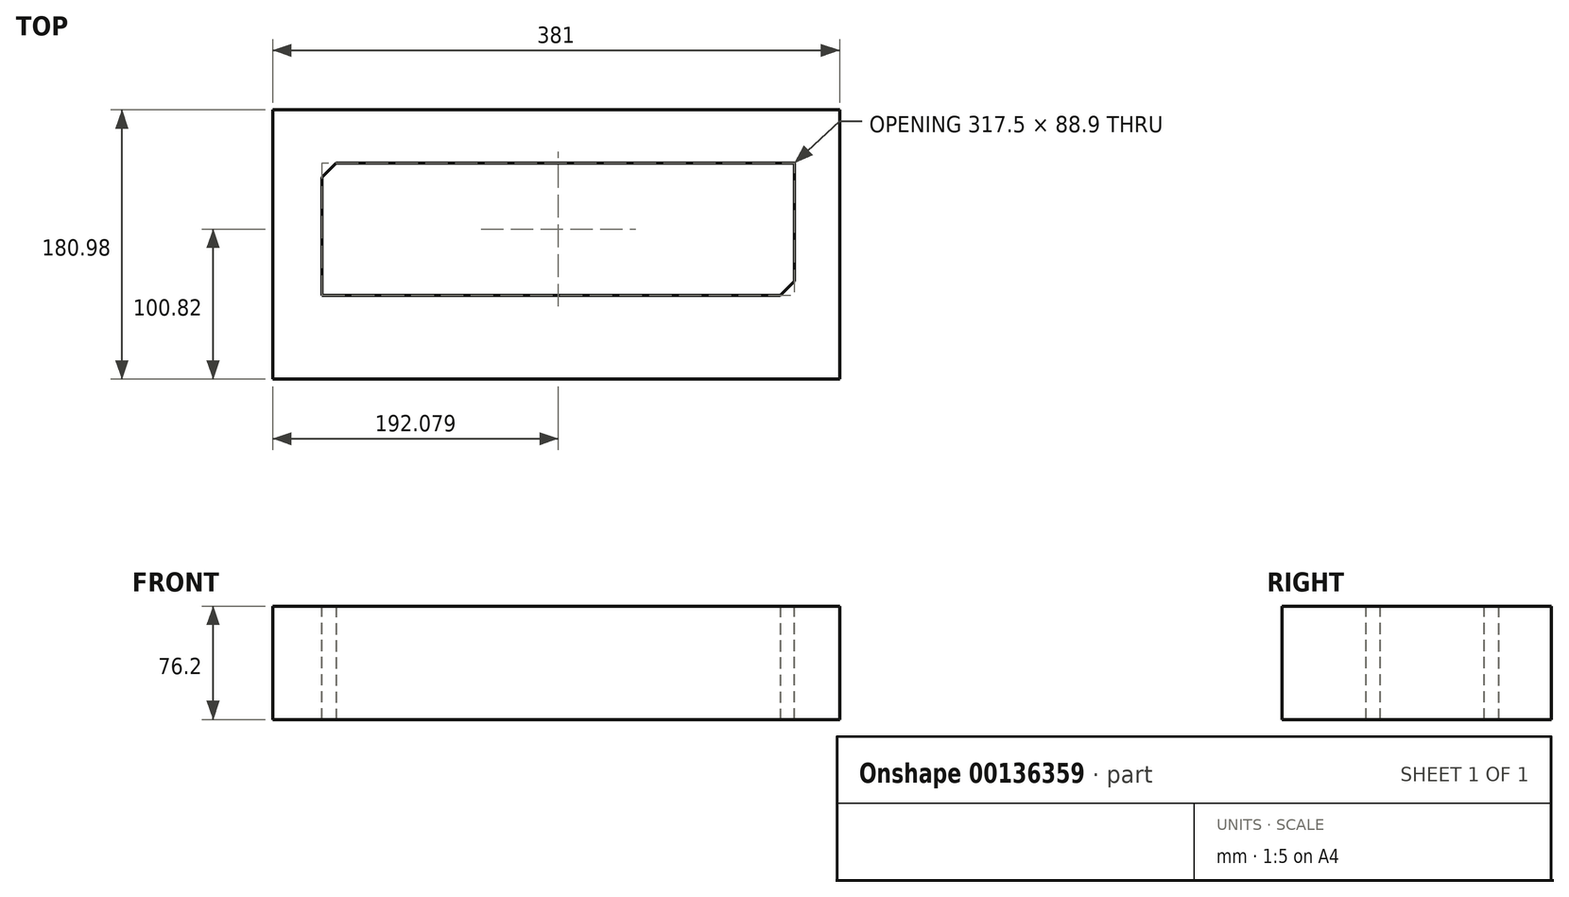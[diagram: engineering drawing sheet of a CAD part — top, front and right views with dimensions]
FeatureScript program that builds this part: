
annotation { "Feature Type Name" : "Feature", "Feature Type Description" : "" }
export const myFeature = defineFeature(function(context is Context, id is Id, definition is map)
    precondition{}
    {
        {
            var Q0;
            Q0=qCreatedBy(makeId("Top.planeOp"),FACE);
            var sketch = newSketch(context, id + "F0", { "sketchPlane" : qUnion([Q0])});
            skLineSegment(sketch, "E0", {"start": v(-193.33, 124.6) * mm, "end": v(187.67, 124.6) * mm});
            skLineSegment(sketch, "E1", {"start": v(187.67, 124.6) * mm, "end": v(187.67, -56.37) * mm});
            skLineSegment(sketch, "E2", {"start": v(187.67, -56.37) * mm, "end": v(-193.33, -56.37) * mm});
            skLineSegment(sketch, "E3", {"start": v(-193.33, -56.37) * mm, "end": v(-193.33, 124.6) * mm});
            skSolve(sketch);
        }
        {
            var Q0;
            Q0 = qSketchRegion(id + "F0", true);
            extrude(context, id + "F1", {"entities" : qUnion([Q0]), "depth" : 76.2 * mm});
        }
        {
            var Q0;
            Q0=makeQuery(id+"F1.opExtrude","CAP_FACE",FACE,{"disambiguationData":[OSD([sQuery(id+"F0.wireOp",EDGE,"E0"),sQuery(id+"F0.wireOp",EDGE,"E1"),sQuery(id+"F0.wireOp",EDGE,"E2"),sQuery(id+"F0.wireOp",EDGE,"E3")])],"isStart":false});
            var sketch = newSketch(context, id + "F2", { "sketchPlane" : qUnion([Q0])});
            skLineSegment(sketch, "E4.bottom", {"start": v(-160, 88.9) * mm, "end": v(157.5, 88.9) * mm});
            skLineSegment(sketch, "E4.top", {"start": v(-160, 0) * mm, "end": v(157.5, 0) * mm});
            skLineSegment(sketch, "E4.left", {"start": v(-160, 88.9) * mm, "end": v(-160, 0) * mm});
            skLineSegment(sketch, "E4.right", {"start": v(157.5, 88.9) * mm, "end": v(157.5, 0) * mm});
            skSolve(sketch);
        }
        {
            var Q0;
            Q0=makeQuery(id+"F2.imprint","IMPRINT",FACE,{"disambiguationData":[TD([[makeQuery(id+"F2.imprint","IMPRINT",EDGE,{"derivedFrom":sQuery(id+"F2.wireOp",EDGE,"E4.bottom")}),-1.0]])]});
            extrude(context, id + "F3", {"entities" : qUnion([Q0]), "operationType" : NewBodyOperationType.REMOVE, "oppositeDirection" : true, "depth" : 76.2 * mm});
        }
        {
            var Q0;
            Q0=makeQuery(id+"F3.boolean.opBoolean","COPY",EDGE,{"derivedFrom":makeQuery(id+"F3.opExtrude","SWEPT_EDGE",EDGE,{"disambiguationData":[OSD([sQuery(id+"F2.wireOp",EDGE,"E4.bottom"),sQuery(id+"F2.wireOp",EDGE,"E4.left")])]})});
            chamfer(context, id + "F4", {"entities" : qUnion([Q0]), "width" : 9.52 * mm, "tangentPropagation" : true});
        }
        {
            var Q0;
            Q0=makeQuery(id+"F3.boolean.opBoolean","COPY",EDGE,{"derivedFrom":makeQuery(id+"F3.opExtrude","SWEPT_EDGE",EDGE,{"disambiguationData":[OSD([sQuery(id+"F2.wireOp",EDGE,"E4.top"),sQuery(id+"F2.wireOp",EDGE,"E4.right")])]})});
            chamfer(context, id + "F5", {"entities" : qUnion([Q0]), "width" : 9.52 * mm, "tangentPropagation" : true});
        }
    });
